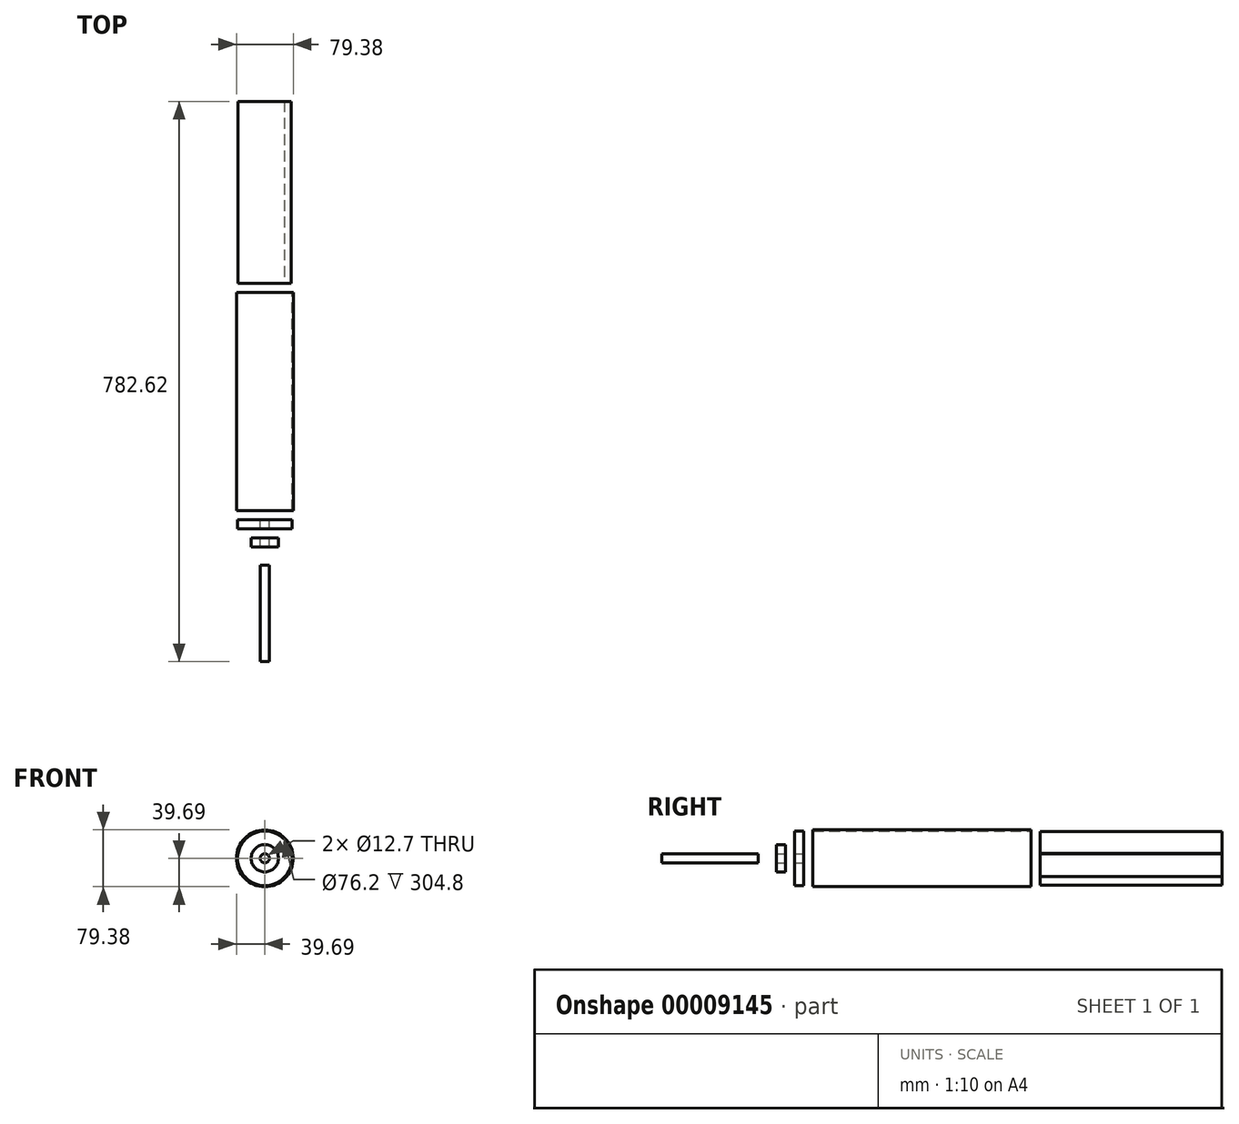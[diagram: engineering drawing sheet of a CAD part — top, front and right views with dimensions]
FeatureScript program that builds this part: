
annotation { "Feature Type Name" : "Feature", "Feature Type Description" : "" }
export const myFeature = defineFeature(function(context is Context, id is Id, definition is map)
    precondition{}
    {
        {
            var Q0;
            Q0=qCreatedBy(makeId("Front.planeOp"),FACE);
            var sketch = newSketch(context, id + "F0", { "sketchPlane" : qUnion([Q0])});
            skCircle(sketch, "E0", {"center": v(0, 0) * mm, "radius": 39.69 * mm});
            skCircle(sketch, "E1", {"center": v(0, 0) * mm, "radius": 38.1 * mm});
            skSolve(sketch);
        }
        {
            var Q0;
            Q0=makeQuery(id+"F0.imprint","IMPRINT",FACE,{"disambiguationData":[TD([[makeQuery(id+"F0.imprint","IMPRINT",EDGE,{"derivedFrom":sQuery(id+"F0.wireOp",EDGE,"E0")}),1.0]])]});
            extrude(context, id + "F1", {"entities" : qUnion([Q0]), "depth" : 127 * mm, "hasSecondDirection" : true, "secondDirectionOppositeDirection" : true, "secondDirectionDepth" : 177.8 * mm});
        }
        {
            var Q0;
            Q0=makeQuery(id+"F1.opExtrude","CAP_FACE",FACE,{"disambiguationData":[OSD([sQuery(id+"F0.wireOp",EDGE,"E0"),sQuery(id+"F0.wireOp",EDGE,"E1")])],"isStart":false});
            cPlane(context, id + "F2", {"entities" : qUnion([Q0]), "cplaneType" : CPlaneType.OFFSET, "offset" : 12.7 * mm, "width" : 152.4 * mm, "height" : 152.4 * mm});
        }
        {
            var Q0;
            Q0=qCreatedBy(id+"F2.planeOp",FACE);
            var sketch = newSketch(context, id + "F3", { "sketchPlane" : qUnion([Q0])});
            skCircle(sketch, "E2", {"center": v(0, 0) * mm, "radius": 38.1 * mm});
            skCircle(sketch, "E3", {"center": v(0, 0) * mm, "radius": 6.35 * mm});
            skSolve(sketch);
        }
        {
            var Q0;
            Q0=makeQuery(id+"F3.imprint","IMPRINT",FACE,{"disambiguationData":[TD([[makeQuery(id+"F3.imprint","IMPRINT",EDGE,{"derivedFrom":sQuery(id+"F3.wireOp",EDGE,"E2")}),1.0]])]});
            extrude(context, id + "F4", {"entities" : qUnion([Q0]), "depth" : 12.7 * mm});
        }
        {
            var Q0;
            Q0=makeQuery(id+"F4.opExtrude","CAP_FACE",FACE,{"disambiguationData":[OSD([sQuery(id+"F3.wireOp",EDGE,"E2"),sQuery(id+"F3.wireOp",EDGE,"E3")])],"isStart":false});
            cPlane(context, id + "F5", {"entities" : qUnion([Q0]), "cplaneType" : CPlaneType.OFFSET, "offset" : 50.8 * mm, "width" : 152.4 * mm, "height" : 152.4 * mm});
        }
        {
            var Q0;
            Q0=qCreatedBy(id+"F5.planeOp",FACE);
            var sketch = newSketch(context, id + "F6", { "sketchPlane" : qUnion([Q0])});
            skCircle(sketch, "E4", {"center": v(0, 0) * mm, "radius": 6.35 * mm});
            skSolve(sketch);
        }
        {
            var Q0;
            Q0=makeQuery(id+"F6.imprint","IMPRINT",FACE,{"disambiguationData":[TD([[makeQuery(id+"F6.imprint","IMPRINT",EDGE,{"derivedFrom":sQuery(id+"F6.wireOp",EDGE,"E4")}),1.0]])]});
            extrude(context, id + "F7", {"entities" : qUnion([Q0]), "depth" : 134.92 * mm});
        }
        {
            var Q0;
            Q0=makeQuery(id+"F4.opExtrude","CAP_FACE",FACE,{"disambiguationData":[OSD([sQuery(id+"F3.wireOp",EDGE,"E2"),sQuery(id+"F3.wireOp",EDGE,"E3")])],"isStart":false});
            cPlane(context, id + "F8", {"entities" : qUnion([Q0]), "cplaneType" : CPlaneType.OFFSET, "offset" : 12.7 * mm, "width" : 152.4 * mm, "height" : 152.4 * mm});
        }
        {
            var Q0;
            Q0=qCreatedBy(id+"F8.planeOp",FACE);
            var sketch = newSketch(context, id + "F9", { "sketchPlane" : qUnion([Q0])});
            skCircle(sketch, "E5.0", {"center": v(0, 0) * mm, "radius": 6.35 * mm});
            skCircle(sketch, "E6", {"center": v(0, 0) * mm, "radius": 19.05 * mm});
            skSolve(sketch);
        }
        {
            var Q0;
            Q0=makeQuery(id+"F9.imprint","IMPRINT",FACE,{"disambiguationData":[TD([[makeQuery(id+"F9.imprint","IMPRINT",EDGE,{"derivedFrom":sQuery(id+"F9.wireOp",EDGE,"E5.0")}),-1.0]])]});
            extrude(context, id + "F10", {"entities" : qUnion([Q0]), "depth" : 12.7 * mm});
        }
        {
            var Q0;
            Q0=makeQuery(id+"F1.opExtrude","CAP_FACE",FACE,{"disambiguationData":[OSD([sQuery(id+"F0.wireOp",EDGE,"E0"),sQuery(id+"F0.wireOp",EDGE,"E1")])],"isStart":true});
            cPlane(context, id + "F11", {"entities" : qUnion([Q0]), "cplaneType" : CPlaneType.OFFSET, "offset" : 12.7 * mm, "width" : 152.4 * mm, "height" : 152.4 * mm});
        }
        {
            var Q0;
            Q0=qCreatedBy(id+"F11.planeOp",FACE);
            var sketch = newSketch(context, id + "F12", { "sketchPlane" : qUnion([Q0])});
            skCircle(sketch, "E7.0", {"center": v(0, 0) * mm, "radius": 6.35 * mm});
            skArc(sketch, "E8", {"start": v(-27.19, -25.78) * mm, "mid": v(35.93, 10.62) * mm, "end": v(-36.83, 6.84) * mm});
            skArc(sketch, "E9", {"start": v(-27.35, -25.23) * mm, "mid": v(35.68, 10.55) * mm, "end": v(-36.67, 6.3) * mm});
            skLineSegment(sketch, "E10", {"start": v(-36.83, 6.84) * mm, "end": v(-27.19, -25.78) * mm});
            skSolve(sketch);
        }
        {
            var Q0;
            {var subQ2=sQuery(id+"F12.wireOp",EDGE,"E8");Q0=makeQuery(id+"F12.imprint","IMPRINT",FACE,{"disambiguationData":[TD([[makeQuery(id+"F12.imprint","IMPRINT",EDGE,{"derivedFrom":subQ2}),1.0]])]});}
            extrude(context, id + "F13", {"entities" : qUnion([Q0]), "depth" : 254 * mm});
        }
    });
